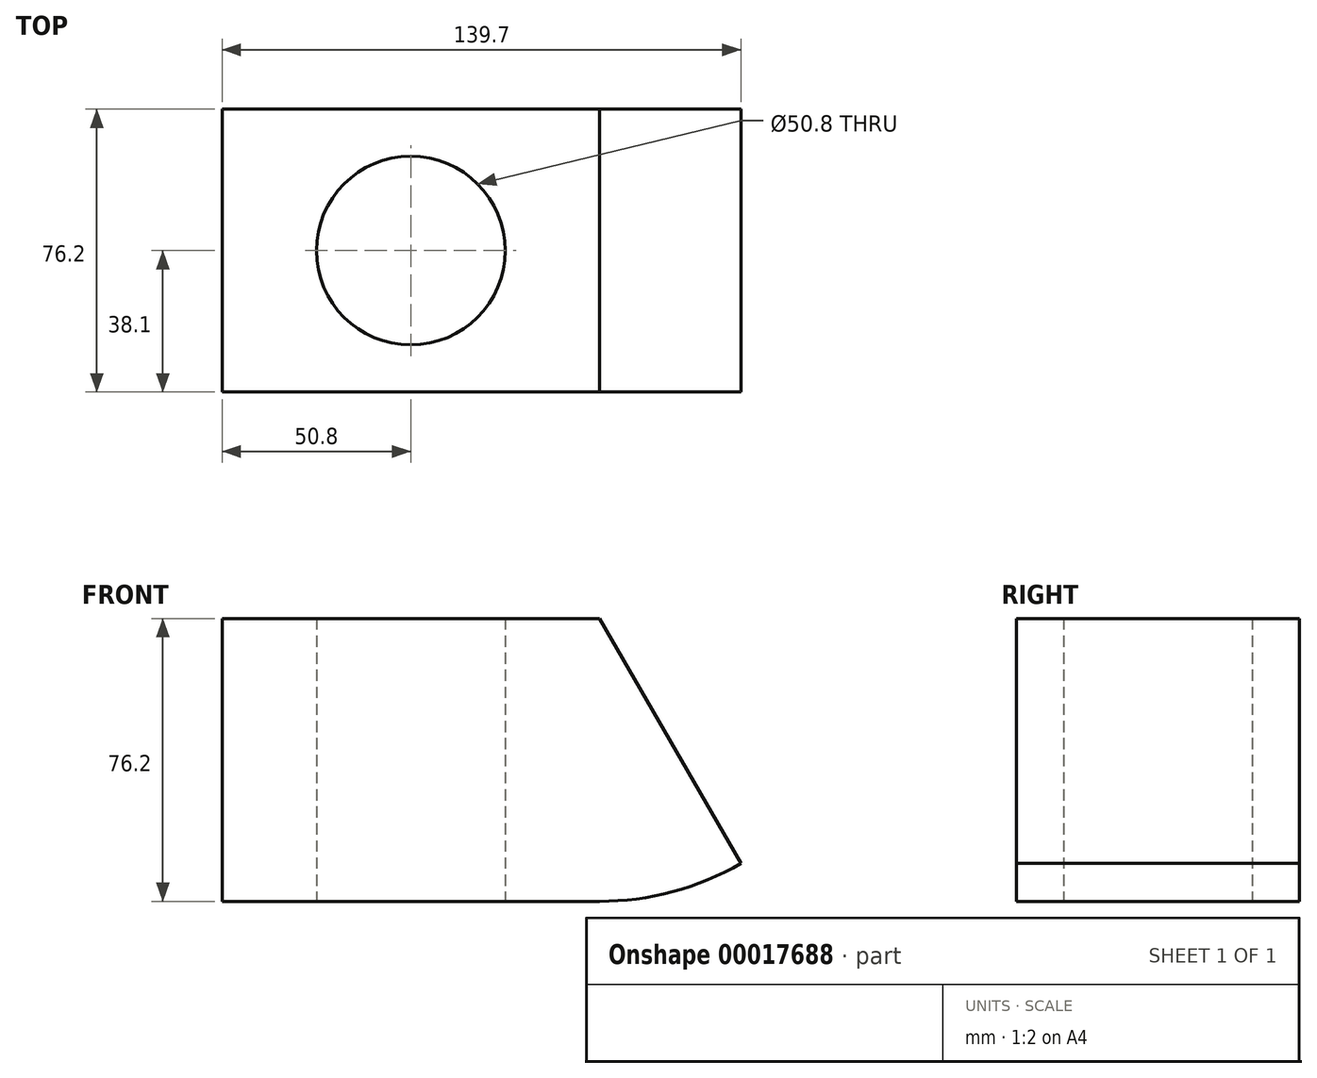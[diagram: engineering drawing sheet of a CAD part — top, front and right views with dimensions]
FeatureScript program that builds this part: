
annotation { "Feature Type Name" : "Feature", "Feature Type Description" : "" }
export const myFeature = defineFeature(function(context is Context, id is Id, definition is map)
    precondition{}
    {
        {
            var Q0;
            Q0=qCreatedBy(makeId("Top.planeOp"),FACE);
            var sketch = newSketch(context, id + "F0", { "sketchPlane" : qUnion([Q0])});
            skLineSegment(sketch, "E0.rect.bottom", {"start": v(50.8, 38.1) * mm, "end": v(-50.8, 38.1) * mm});
            skLineSegment(sketch, "E0.rect.top", {"start": v(50.8, -38.1) * mm, "end": v(-50.8, -38.1) * mm});
            skLineSegment(sketch, "E0.rect.left", {"start": v(50.8, 38.1) * mm, "end": v(50.8, -38.1) * mm});
            skLineSegment(sketch, "E0.rect.right", {"start": v(-50.8, 38.1) * mm, "end": v(-50.8, -38.1) * mm});
            skPoint(sketch, "E0.rect.middle", {"position": v(0, 0) * mm});
            skCircle(sketch, "E1", {"center": v(0, 0) * mm, "radius": 25.4 * mm});
            skSolve(sketch);
        }
        {
            var Q0;
            Q0=makeQuery(id+"F0.imprint","IMPRINT",FACE,{"disambiguationData":[TD([[makeQuery(id+"F0.imprint","IMPRINT",EDGE,{"derivedFrom":sQuery(id+"F0.wireOp",EDGE,"E0.rect.bottom")}),1.0]])]});
            extrude(context, id + "F1", {"entities" : qUnion([Q0]), "depth" : 76.2 * mm});
        }
        {
            var Q0;
            Q0=makeQuery(id+"F1.opExtrude","SWEPT_FACE",FACE,{"disambiguationData":[OSD([sQuery(id+"F0.wireOp",EDGE,"E0.rect.left")])]});
            var sketch = newSketch(context, id + "F2", { "sketchPlane" : qUnion([Q0])});
            skLineSegment(sketch, "E2.0", {"start": v(38.1, 76.2) * mm, "end": v(-38.1, 76.2) * mm});
            skSolve(sketch);
        }
        {
            var Q0;
            Q0=makeQuery(id+"F2.imprint","IMPRINT",FACE,{"disambiguationData":[TD([[makeQuery(id+"F2.imprint","IMPRINT",EDGE,{"derivedFrom":sQuery(id+"F2.wireOp",EDGE,"E2.0")}),1.0]])]});
            var Q1;
            Q1=sQuery(id+"F2.wireOp",EDGE,"E2.0");
            revolve(context, id + "F3", {"operationType" : NewBodyOperationType.ADD, "entities" : qUnion([Q0]), "axis" : qUnion([Q1]), "revolveType" : RevolveType.ONE_DIRECTION, "angle" : 30 * degree});
        }
    });
